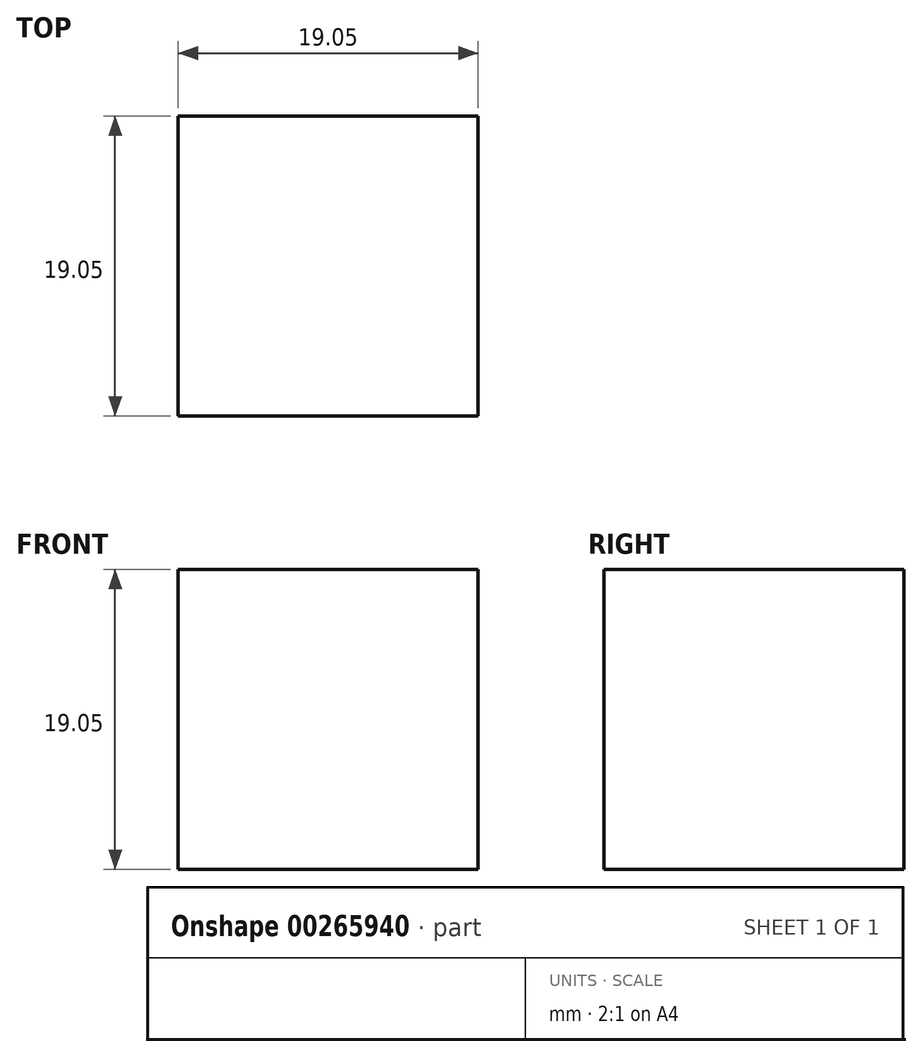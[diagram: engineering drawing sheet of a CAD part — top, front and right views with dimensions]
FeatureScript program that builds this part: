
annotation { "Feature Type Name" : "Feature", "Feature Type Description" : "" }
export const myFeature = defineFeature(function(context is Context, id is Id, definition is map)
    precondition{}
    {
        {
            var Q0;
            Q0=qCreatedBy(makeId("Front.planeOp"),FACE);
            var sketch = newSketch(context, id + "F0", { "sketchPlane" : qUnion([Q0])});
            skLineSegment(sketch, "E0", {"start": v(-34.23, 19.34) * mm, "end": v(-14.55, 19.34) * mm});
            skLineSegment(sketch, "E1", {"start": v(-14.55, 19.34) * mm, "end": v(-14.55, 0.29) * mm});
            skLineSegment(sketch, "E2", {"start": v(-14.55, 0.29) * mm, "end": v(-33.6, 0.29) * mm});
            skLineSegment(sketch, "E3", {"start": v(-33.6, 0.29) * mm, "end": v(-33.6, 19.34) * mm});
            skSolve(sketch);
        }
        {
            var Q0;
            Q0 = qSketchRegion(id + "F0", true);
            extrude(context, id + "F1", {"entities" : qUnion([Q0]), "depth" : 19.05 * mm});
        }
    });
